# Revit family: IS_Conca_T3968_BIM_IT
name_source: partatom
category: Plumbing Fixtures
revit_build: Autodesk Revit 2017 (Build: 20160225_1515(x64)
units: mm (PartAtom-declared; Revit-internal decimal feet)

## family parameters
Always vertical = No
Cut with Voids When Loaded = No
OmniClass Number = 23.45.05.14.21.11
OmniClass Title = Bath/Shower Units
Part Type = Normal
Room Calculation Point = No
Round Connector Dimension = Use Diameter
Shared = No
Work Plane-Based = No

## types (1)
- T3968BH - MIRROR SQUARED  120
    Accessori = https://www.idealstandard.it
    Aiuto = https://www.idealstandard.it
    AltezzaNominale = 30 mm  [stored 0.0984252 ft]
    Autore = Ideal Standard
    BIMobject category = Storage
    BIMobject category code = sanitary-storage
    BIMobject main category = Sanitary
    BIMobject main category code = sanitary
    Brand = https://www.idealstandard.it
    Caratteristiche = Specchio quadrato  1200 x 1200 mm con cornice esterna in alluminio nera (195x195x37)
    CodiceABarre = 8014140461869
    CodiceArticolo = T3968BH
    Colore = Mirror
    CostoDiSostituzione = 0 $
    Description = 1200 x 1200 mm Square-Mirror with outer frame in black aluminum (195x195x37)
    DescrizioneClassifcazioneUni2015 = Bathroom cabinets
    Desrizione = Specchio quadrato  1200 x 1200 mm con cornice esterna in alluminio nera (195x195x37)
    DimensioneScarico = 0
    DurataGaranzia = 2
    DurataGaranziaProdotti = 2
    Finitura = Mirror
    Forma = Rettangolare
    Garanzia = Garanzia Idealstandard
    IfcEsportaCome = IfcFurnitureType
    InformaziniGaranzia = https://www.idealstandard.it
    InformazioniDiProdotto = http://www.idealstandard.it
    InformazioniGaranzia = https://www.idealstandard.it
    Installation instructions = https://www.idealspec.co.uk
    InstruzioniInstallazione = https://www.idealstandard.it
    LarghezzaNominale = 1200 mm
    LunghezzaNominale = 0 mm  [stored 0 ft]
    Maniglia = No
    Manufacturer = Ideal Standard
    Materiale = Ceramics
    Model = T3968BH
    ModelloDiRiferimento = T3968BH
    Nome = BathroomCabinets_Conca_T3968BH_IdealStandard
    NomeOggettoBim = ISI_IdealStandard_Bathroom Cabinets_Conca_T3968BH
    Nominal depth = 0
    Nominal height = 0
    NominalDepth = 37 mm
    NominalHeight = 1200 mm
    NominalWidth = 1200 mm
    NumeroDiModello = T3968BH
    PesoNetto = 17
    PiattoDoccia = No
    Product group = Bathroom_Furniture
    Produttore = Ideal Standard
    ProfonditaNominale = 1200 mm
    Revisione = 1
    RiferimentoClassificazioneUni2015 = Pr_40_30_78_03
    SeatMaterial = 0 mm  [stored 0 ft]
    Spazio = Interno
    SpessoreDelMateriale = 0
    SpilloverLivello = 0
    Telefono = 800 652 290
    TipoEspotazioneIfc = Bathroom cabinets
    URL = https://www.ideal-standard.co.uk
    Uniclass 2015 Code = Pr_40_30_78_03
    Uniclass 2015 Name = Bathroom cabinets
    UnitàDurata = Anno
    UnitàDurataGaranzia = Anno
    UnitàLineare = Milimitre
    UnitàMonetaria = €
    UnitàSuperficie = Milimitre
    UnitàVolume = Litri
    Versione = 1
    VersioneClassificazioneUni2015 = v1.1
    Weight Net (Kg) = 0

note: [stored X ft] marks values corroborated as IEEE doubles in the binary element streams (Revit-internal decimal feet)

## geometry (parser evidence)
native form markers: Sweep x2
no freeform markers — native parametric forms only
